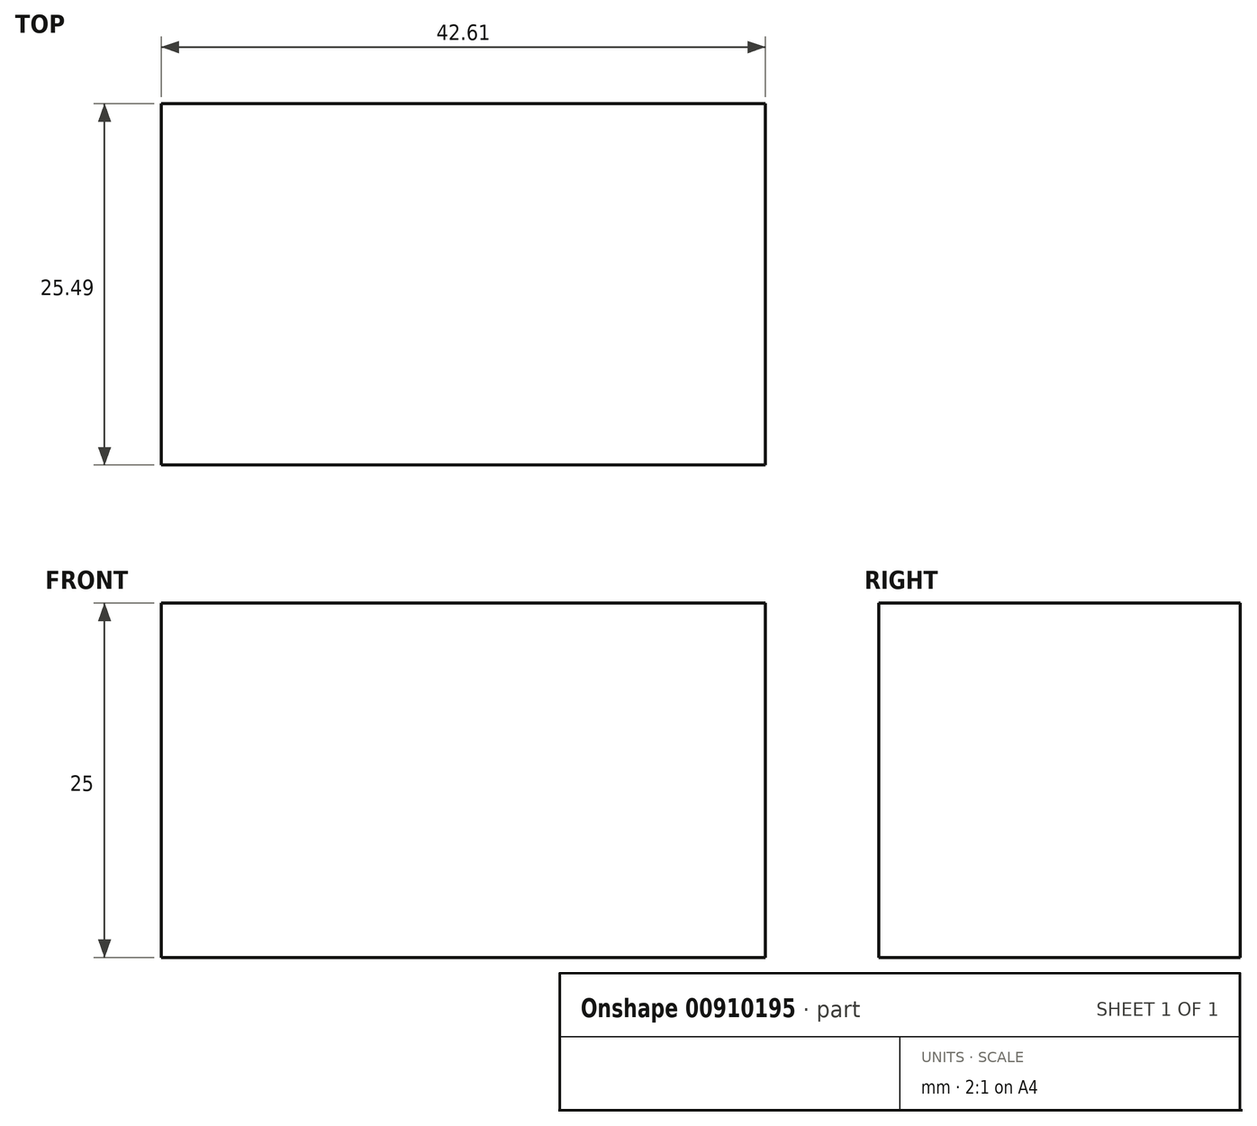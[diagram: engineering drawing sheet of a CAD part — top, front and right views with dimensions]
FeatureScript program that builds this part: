
annotation { "Feature Type Name" : "Feature", "Feature Type Description" : "" }
export const myFeature = defineFeature(function(context is Context, id is Id, definition is map)
    precondition{}
    {
        {
            var Q0;
            Q0=qCreatedBy(makeId("Top.planeOp"),FACE);
            var sketch = newSketch(context, id + "F0", { "sketchPlane" : qUnion([Q0])});
            skLineSegment(sketch, "E0", {"start": v(-148.68, -60.44) * mm, "end": v(-30.28, -158.86) * mm});
            skLineSegment(sketch, "E1.bottom", {"start": v(-55.72, 45.13) * mm, "end": v(-13.1, 45.13) * mm});
            skLineSegment(sketch, "E1.top", {"start": v(-55.72, 19.64) * mm, "end": v(-13.1, 19.64) * mm});
            skLineSegment(sketch, "E1.left", {"start": v(-55.72, 45.13) * mm, "end": v(-55.72, 19.64) * mm});
            skLineSegment(sketch, "E1.right", {"start": v(-13.1, 45.13) * mm, "end": v(-13.1, 19.64) * mm});
            skSolve(sketch);
        }
        {
            var Q0;
            Q0 = qSketchRegion(id + "F0", true);
            extrude(context, id + "F1", {"entities" : qUnion([Q0]), "depth" : 25 * mm, "offsetDistance" : 25 * mm});
        }
    });
